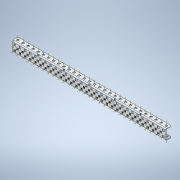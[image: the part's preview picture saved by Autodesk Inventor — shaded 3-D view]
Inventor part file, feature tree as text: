
AUTODESK INVENTOR PART (.ipt)
format: ipt  version: 2020 (Build 240168000, 168)  size: 1,512,448 bytes
history: native  units: in
note: dims shown in document units (in); Inventor stores cm internally (conversion verified against a paired STEP export)
features: other x153, plane x7, pattern_linear x4, split x1, sheet_metal_op x1
ambient origin geometry x8: Origin, YZ Plane, XZ Plane, XY Plane, X Axis, Y Axis, Z Axis, Center Point
bodies: Solid1 (feature_tree)
feature tree (166):
  other  "Work Axis1"
  pattern_linear  "Rectangular Pattern1"  Count1=30 Spacing1=0.5in
  other  "Work Axis72"
  pattern_linear  "Rectangular Pattern2"  Count1=30 Spacing1=0.5in
  pattern_linear  "Rectangular Pattern3"  Count1=30 Spacing1=0.5in
  other  "Work Axis141"
  pattern_linear  "Rectangular Pattern4"  Count1=29 Spacing1=0.5in
  plane  "Work Plane7"
  split  "Split1"
  plane  "Work Plane1"
  plane  "Work Plane2"
  other  "Work Point1"
  other  "Work Axis2"
  other  "Work Axis3"
  other  "Work Axis4"
  other  "Work Axis5"
  other  "Work Axis6"
  other  "Work Axis7"
  other  "Work Axis8"
  other  "Work Axis9"
  other  "Work Axis10"
  other  "Work Axis11"
  other  "Work Axis12"
  other  "Work Axis13"
  other  "Work Axis14"
  other  "Work Axis15"
  other  "Work Axis16"
  other  "Work Axis17"
  other  "Work Axis18"
  other  "Work Axis19"
  other  "Work Axis20"
  other  "Work Axis21"
  other  "Work Axis22"
  other  "Work Axis23"
  other  "Work Axis24"
  other  "Work Axis25"
  other  "Work Axis26"
  other  "Work Axis27"
  other  "Work Axis28"
  other  "Work Axis29"
  other  "Work Axis30"
  other  "Work Axis36"
  other  "Work Axis37"
  other  "Work Axis38"
  other  "Work Axis39"
  other  "Work Axis40"
  other  "Work Axis41"
  other  "Work Axis42"
  other  "Work Axis43"
  other  "Work Axis44"
  other  "Work Axis45"
  other  "Work Axis46"
  other  "Work Axis47"
  other  "Work Axis48"
  other  "Work Axis49"
  other  "Work Axis50"
  other  "Work Axis51"
  other  "Work Axis52"
  other  "Work Axis53"
  other  "Work Axis54"
  other  "Work Axis55"
  other  "Work Axis56"
  other  "Work Axis57"
  other  "Work Axis58"
  other  "Work Axis59"
  other  "Work Axis60"
  other  "Work Axis61"
  other  "Work Axis62"
  other  "Work Axis63"
  other  "Work Axis64"
  other  "Work Axis65"
  plane  "Work Plane3"
  plane  "Work Plane4"
  other  "Work Point2"
  other  "Work Axis71"
  other  "Work Point3"
  other  "Work Axis73"
  other  "Work Axis74"
  other  "Work Axis75"
  other  "Work Axis76"
  other  "Work Axis77"
  other  "Work Axis78"
  other  "Work Axis79"
  other  "Work Axis80"
  other  "Work Axis81"
  other  "Work Axis82"
  other  "Work Axis83"
  other  "Work Axis84"
  other  "Work Axis85"
  other  "Work Axis86"
  other  "Work Axis87"
  other  "Work Axis88"
  other  "Work Axis89"
  other  "Work Axis90"
  other  "Work Axis91"
  other  "Work Axis92"
  other  "Work Axis93"
  other  "Work Axis94"
  other  "Work Axis95"
  other  "Work Axis96"
  other  "Work Axis97"
  other  "Work Axis98"
  other  "Work Axis99"
  other  "Work Axis100"
  other  "Work Axis101"
  other  "Work Axis107"
  other  "Work Axis108"
  other  "Work Axis109"
  other  "Work Axis110"
  other  "Work Axis111"
  other  "Work Axis112"
  other  "Work Axis113"
  other  "Work Axis114"
  other  "Work Axis115"
  other  "Work Axis116"
  other  "Work Axis117"
  other  "Work Axis118"
  other  "Work Axis119"
  other  "Work Axis120"
  other  "Work Axis121"
  other  "Work Axis122"
  other  "Work Axis123"
  other  "Work Axis124"
  other  "Work Axis125"
  other  "Work Axis126"
  other  "Work Axis127"
  other  "Work Axis128"
  other  "Work Axis129"
  other  "Work Axis130"
  other  "Work Axis131"
  other  "Work Axis132"
  other  "Work Axis133"
  other  "Work Axis134"
  other  "Work Axis135"
  plane  "Work Plane5"
  plane  "Work Plane6"
  other  "Work Point4"
  other  "Work Axis142"
  other  "Work Axis143"
  other  "Work Axis144"
  other  "Work Axis145"
  other  "Work Axis146"
  other  "Work Axis147"
  other  "Work Axis148"
  other  "Work Axis149"
  other  "Work Axis150"
  other  "Work Axis151"
  other  "Work Axis152"
  other  "Work Axis153"
  other  "Work Axis154"
  other  "Work Axis155"
  other  "Work Axis156"
  other  "Work Axis157"
  other  "Work Axis158"
  other  "Work Axis159"
  other  "Work Axis160"
  other  "Work Axis161"
  other  "Work Axis162"
  other  "Work Axis163"
  other  "Work Axis164"
  other  "Work Axis165"
  other  "Work Axis166"
  other  "Work Axis167"
  other  "Work Axis168"
  other  "Work Axis169"
  sheet_metal_op  "Fold1"
